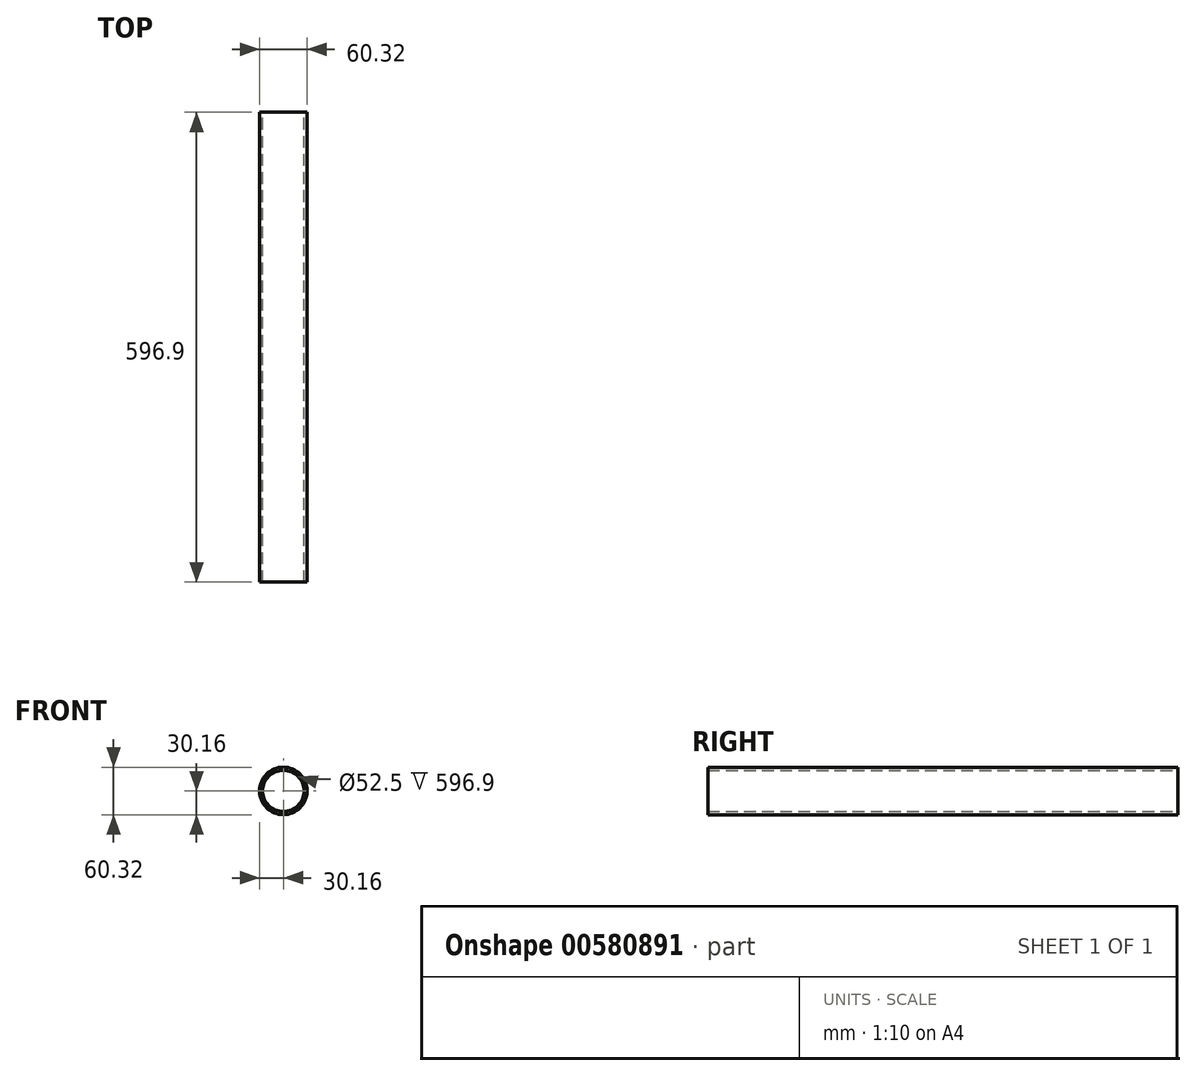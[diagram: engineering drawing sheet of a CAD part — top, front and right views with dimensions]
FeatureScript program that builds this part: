
annotation { "Feature Type Name" : "Feature", "Feature Type Description" : "" }
export const myFeature = defineFeature(function(context is Context, id is Id, definition is map)
    precondition{}
    {
        {
            var Q0;
            Q0=qCreatedBy(makeId("Front.planeOp"),FACE);
            var sketch = newSketch(context, id + "F0", { "sketchPlane" : qUnion([Q0])});
            skCircle(sketch, "E0", {"center": v(0, 0) * mm, "radius": 30.16 * mm});
            skCircle(sketch, "E1.0", {"center": v(0, 0) * mm, "radius": 26.25 * mm});
            skSolve(sketch);
        }
        {
            var Q0;
            Q0 = qSketchRegion(id + "F0", true);
            extrude(context, id + "F1", {"entities" : qUnion([Q0]), "endBound" : BoundingType.SYMMETRIC, "depth" : 596.9 * mm, "offsetDistance" : 25 * mm});
        }
    });
